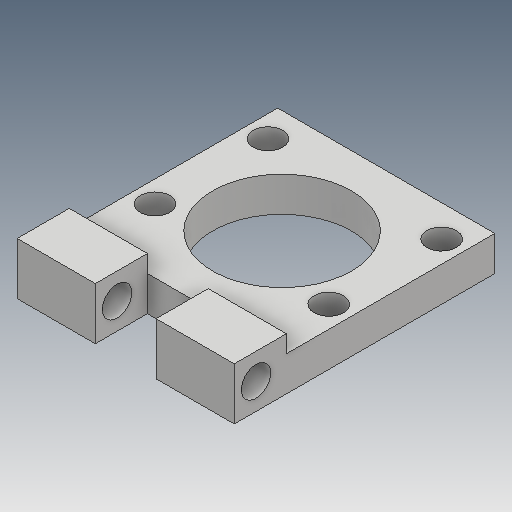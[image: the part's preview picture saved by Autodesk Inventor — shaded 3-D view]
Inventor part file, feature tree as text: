
AUTODESK INVENTOR PART (.ipt)
format: ipt  version: 2018 (Build 220112000, 112)  size: 176,640 bytes
history: native  units: mm
features: extrude x6, sketch x6, projected_geometry x1
ambient origin geometry x8: Origin, YZ Plane, XZ Plane, XY Plane, X Axis, Y Axis, Z Axis, Center Point
bodies: Volumenkörper1 (feature_tree)
feature tree (13):
  extrude  "Extrusion1"  Depth=25.0mm
  extrude  "Extrusion2"  Depth=16.0mm
  extrude  "Extrusion4"  Depth=18.0mm
  extrude  "Extrusion5"  Depth=10.0mm
  extrude  "Extrusion6"  Depth=2.5mm
  extrude  "Extrusion7"  Depth=2.0mm
  sketch  "Skizze1"  dims[d0=30.0mm d1=25.0mm]
  sketch  "Skizze2"  dims[d2=6.0mm d3=0.0mm d4=16.0mm]
  sketch  "Skizze4"  dims[d5=12.5mm d6=18.0mm]
  sketch  "Skizze6"  dims[d7=10.0mm d8=0.0mm d12=20.0mm]
  sketch  "Skizze7"  dims[d13=13.0mm d14=2.5mm]
  sketch  "Skizze8"  dims[d15=3.4mm d16=3.4mm d17=3.4mm d18=3.4mm d19=10.0mm d20=0.0mm d21=9.0mm d22=9.0mm d23=6.0mm d24=10.0mm d25=0.0mm d26=3.4mm d27=3.0mm d28=2.5mm d29=40.0mm d30=0.0mm d31=2.0mm d32=0.0mm]
  projected_geometry  "Projizierte Kontur1"
